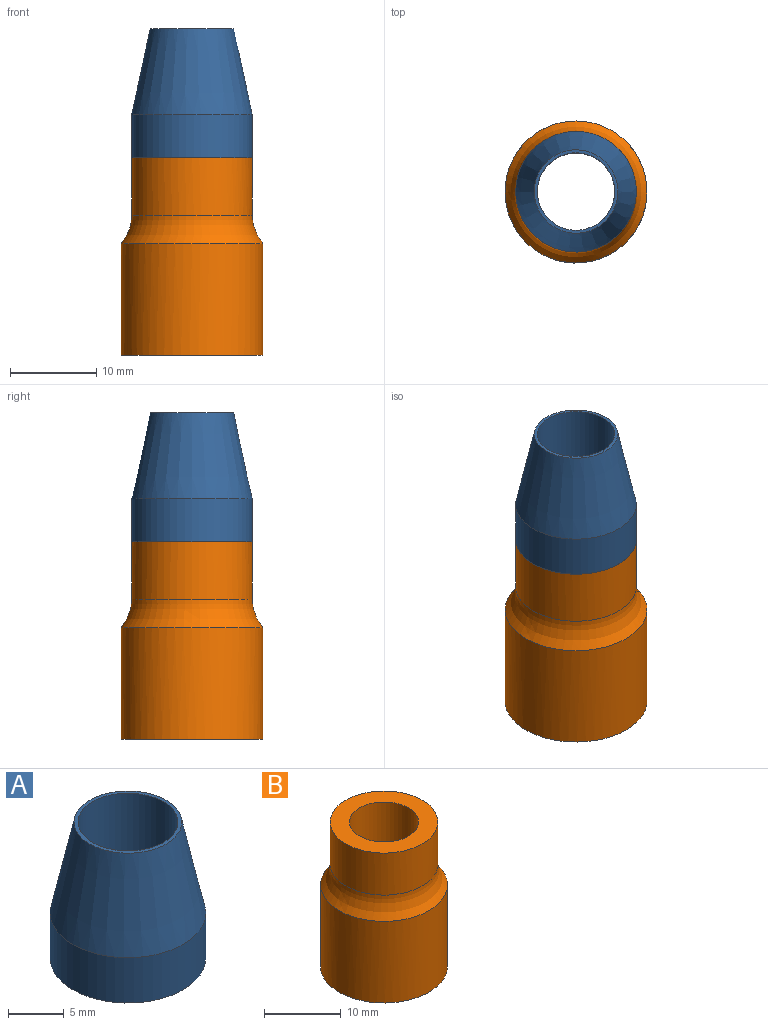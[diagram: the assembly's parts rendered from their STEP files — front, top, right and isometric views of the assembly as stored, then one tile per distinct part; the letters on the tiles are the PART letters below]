
ASSEMBLY  parts=2 mates=1
PART A: 5 faces, bbox 14x14x15 mm
  f0: plane 9.7x9.7mm, normal (0,0,1), area 10.3mm2, adj f1,f4
  f1: cone r=4.85mm half-angle=12.1deg, axis (0,0,-1), area 380.8mm2, adj f0,f2
  f2: cylinder r=7mm len=14mm, axis (0,0,1), area 219.9mm2, adj f1,f3
  f3: plane 14x14mm, normal (0,0,-1), area 90.3mm2, adj f2,f4
  f4: cylinder r=4.5mm len=15mm, axis (0,0,-1), area 424.1mm2, adj f0,f3
PART B: 8 faces, bbox 18.3x18.3x23 mm
  f0: cylinder r=6.75mm len=13.5mm, axis (0,0,-1), area 424.1mm2, adj f2,f3
  f1: cylinder r=8.25mm len=16.5mm, axis (0,0,-1), area 673.9mm2, adj f2,f7
  f2: plane 16.5x16.5mm, normal (0,0,-1), area 70.7mm2, adj f0,f1
  f3: plane 13.5x13.5mm, normal (0,0,-1), area 79.5mm2, adj f0,f4
  f4: cylinder r=4.5mm len=13mm, axis (0,0,-1), area 367.6mm2, adj f3,f6
  f5: cylinder r=7mm len=14mm, axis (0,0,-1), area 294.4mm2, adj f6,f7
  f6: plane 14x14mm, normal (0,0,1), area 90.3mm2, adj f4,f5
  f7: torus R=12mm, axis (0,0,-1), area 168.6mm2, adj f1,f5
PLACE A t=(0.49,21.27,31.85)mm
PLACE B t=(0.49,21.27,3.85)mm
MATE fastened B.f0 <-> A.f1  axis (0,0,1) through (0.49,21.27,26.85)mm
